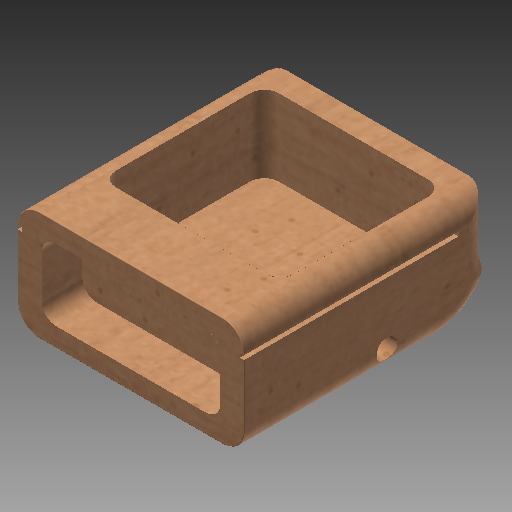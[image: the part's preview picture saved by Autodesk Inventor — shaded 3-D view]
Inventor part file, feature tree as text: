
AUTODESK INVENTOR PART (.ipt)
format: ipt  version: 2018 (Build 220112000, 112)  size: 440,320 bytes
history: native  units: in
note: dims shown in document units (in); Inventor stores cm internally (conversion verified against a paired STEP export)
features: sketch x5, extrude x5, fillet x4, hole x2, mirror x1
ambient origin geometry x8: Origin, YZ Plane, XZ Plane, XY Plane, X Axis, Y Axis, Z Axis, Center Point
bodies: Solid1 (feature_tree)
feature tree (17):
  sketch  "Sketch1"  dims[d0=3.17in d1=1.53in]
  extrude  "Extrusion1"  Depth=1.53in
  extrude  "Extrusion5"  Depth=0.2in
  extrude  "Extrusion3"  Depth=1.0in
  extrude  "Extrusion4"  Depth=0.837in
  extrude  "Extrusion6"  Depth=2.5in
  fillet  "Fillet1"  Radius=1.07in
  fillet  "Fillet2"  Radius=0.06in
  fillet  "Fillet3"  Radius=0.3in
  hole  "Hole1"  [1 undecoded]
  hole  "Hole2"  [1 undecoded]
  mirror  "Mirror1"
  fillet  "Fillet4"  Radius=0.75in
  sketch  "Sketch3"  dims[d2=3.5in d3=0.0in d9=0.2in]
  sketch  "Sketch4"  dims[d10=2.5in d11=1.0in]
  sketch  "Sketch5"  dims[d12=0.57in d13=0.0in d15=0.837in]
  sketch  "Sketch6"  dims[d16=2.28in d17=2.5in d18=1.07in d19=0.0in d20=0.06in d21=0.3in d23=3.0in d24=0.0in d25=0.05in d26=0.75in d27=0.983in d28=3.0in d29=0.0in d30=0.75in d31=0.3in d32=0.3in d33=0.1in d34=0.28in d35=0.28in d36=2.8in d37=0.2in d38=0.75in d39=0.375in d40=0.25in d41=0.5635in d42=0.125in d43=0.8108in d44=2.0in d45=0.3in d46=0.29in d47=0.75in d48=0.375in d49=0.25in d50=0.5635in d51=0.35in d52=0.8108in d53=0.01in]
note: 2 required parameter values undecoded (feature->parameter linkage not recoverable at this tier; creation-order binding heuristic only, values carry confidence <= 0.55)
